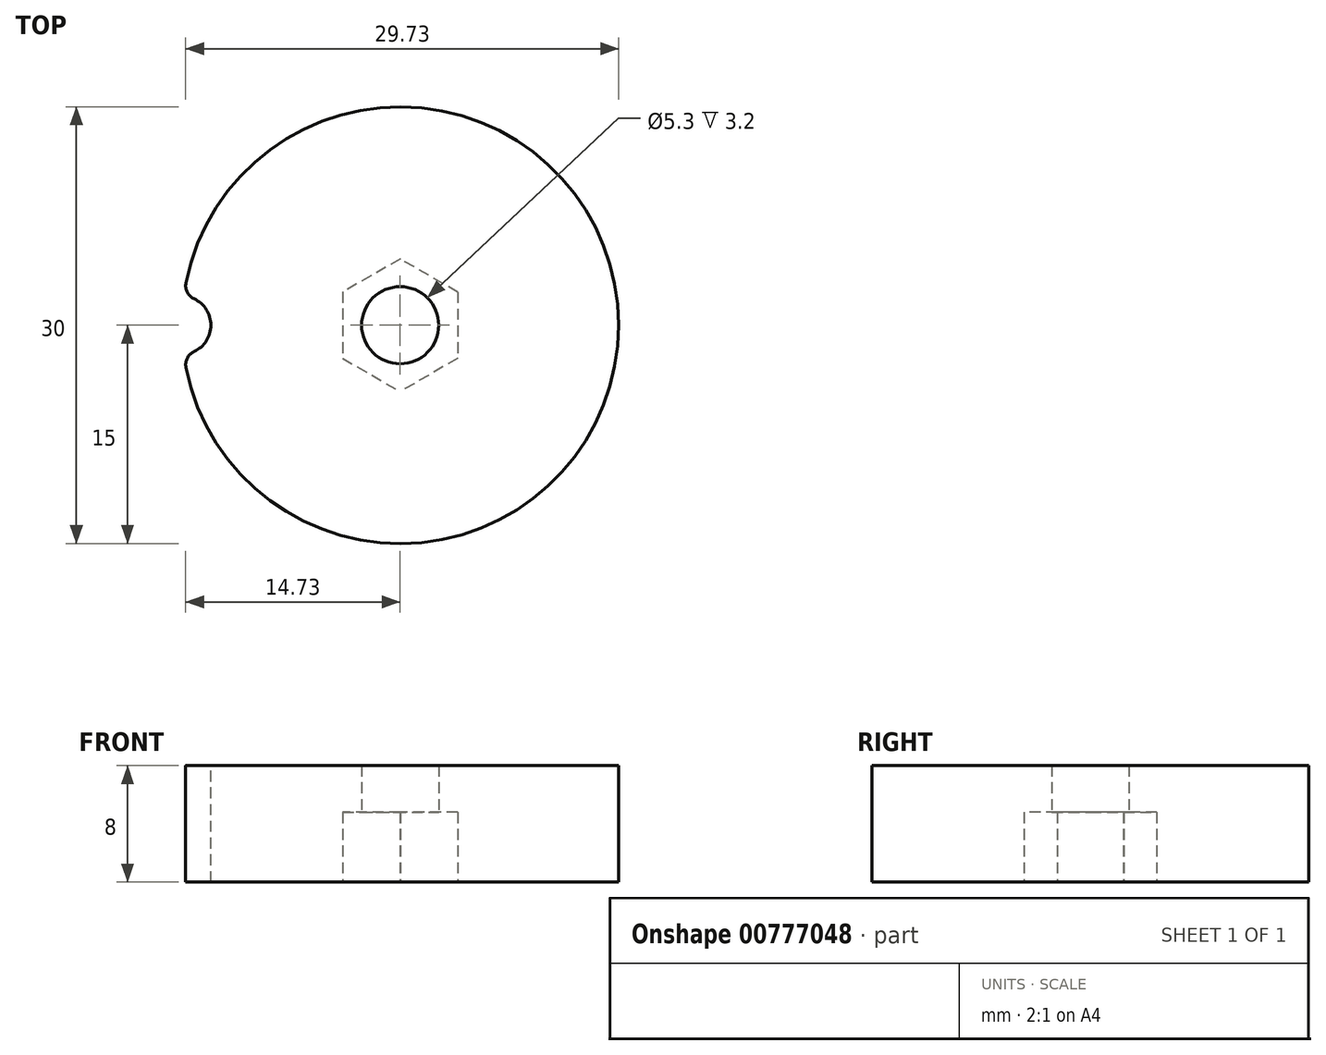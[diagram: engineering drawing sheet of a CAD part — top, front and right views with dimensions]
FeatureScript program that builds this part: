
annotation { "Feature Type Name" : "Feature", "Feature Type Description" : "" }
export const myFeature = defineFeature(function(context is Context, id is Id, definition is map)
    precondition{}
    {
        {
            var Q0;
            Q0=qCreatedBy(makeId("Top.planeOp"),FACE);
            var sketch = newSketch(context, id + "F0", { "sketchPlane" : qUnion([Q0])});
            skCircle(sketch, "E0", {"center": v(0, 0) * mm, "radius": 15 * mm});
            skCircle(sketch, "E1", {"center": v(0, 0) * mm, "radius": 2.65 * mm});
            skSolve(sketch);
        }
        {
            var Q0;
            Q0=qSketchRegion(id+"F0",true);
            extrude(context, id + "F1", {"entities" : qUnion([Q0]), "depth" : 8 * mm});
        }
        {
            var Q0;
            Q0=makeQuery(id+"F1.opExtrude","CAP_FACE",FACE,{"disambiguationData":[OSD([sQuery(id+"F0.wireOp",EDGE,"E0"),sQuery(id+"F0.wireOp",EDGE,"E1")])],"isStart":true});
            var sketch = newSketch(context, id + "F2", { "sketchPlane" : qUnion([Q0])});
            skPoint(sketch, "E2", {"position": v(0, 0) * mm});
            skCircle(sketch, "E3.0", {"center": v(0, 0) * mm, "radius": 2.65 * mm, "construction": true});
            skCircle(sketch, "E4", {"center": v(0, 0) * mm, "radius": 3.95 * mm, "construction": true});
            skLineSegment(sketch, "E5", {"start": v(-3.95, -2.29) * mm, "end": v(-3.95, 2.27) * mm});
            skLineSegment(sketch, "E6", {"start": v(-3.95, 2.27) * mm, "end": v(0, 4.56) * mm});
            skLineSegment(sketch, "E7", {"start": v(3.96, -2.28) * mm, "end": v(0, -4.56) * mm});
            skLineSegment(sketch, "E8", {"start": v(0, -4.56) * mm, "end": v(-3.95, -2.29) * mm});
            skLineSegment(sketch, "E9", {"start": v(3.96, -2.28) * mm, "end": v(3.94, 2.28) * mm});
            skLineSegment(sketch, "E10", {"start": v(3.94, 2.28) * mm, "end": v(0, 4.56) * mm});
            skSolve(sketch);
        }
        {
            var Q0;
            Q0=qSketchRegion(id+"F2",true);
            extrude(context, id + "F3", {"entities" : qUnion([Q0]), "operationType" : NewBodyOperationType.REMOVE, "oppositeDirection" : true, "depth" : 4.8 * mm});
        }
        {
            var Q0;
            Q0=makeQuery(id+"F1.opExtrude","CAP_FACE",FACE,{"disambiguationData":[OSD([sQuery(id+"F0.wireOp",EDGE,"E0"),sQuery(id+"F0.wireOp",EDGE,"E1")])],"isStart":false});
            var sketch = newSketch(context, id + "F4", { "sketchPlane" : qUnion([Q0])});
            skCircle(sketch, "E11", {"center": v(-15, 0) * mm, "radius": 2 * mm});
            skSolve(sketch);
        }
        {
            var Q0;
            Q0=qSketchRegion(id+"F4",true);
            extrude(context, id + "F5", {"entities" : qUnion([Q0]), "operationType" : NewBodyOperationType.REMOVE, "endBound" : BoundingType.THROUGH_ALL, "oppositeDirection" : true, "depth" : 25 * mm});
        }
        {
            var Q0;
            Q0=makeQuery(id+"F5.boolean.opBoolean","INTERSECT",EDGE,{"disambiguationData":[OD(1.0)],"derivedFrom":[makeQuery(id+"F1.opExtrude","SWEPT_FACE",FACE,{"disambiguationData":[OSD([sQuery(id+"F0.wireOp",EDGE,"E0")])]}),makeQuery(id+"F5.opExtrude","SWEPT_FACE",FACE,{"disambiguationData":[OSD([sQuery(id+"F4.wireOp",EDGE,"E11")])]})]});
            var Q1;
            Q1=makeQuery(id+"F5.boolean.opBoolean","INTERSECT",EDGE,{"disambiguationData":[OD(0.0)],"derivedFrom":[makeQuery(id+"F1.opExtrude","SWEPT_FACE",FACE,{"disambiguationData":[OSD([sQuery(id+"F0.wireOp",EDGE,"E0")])]}),makeQuery(id+"F5.opExtrude","SWEPT_FACE",FACE,{"disambiguationData":[OSD([sQuery(id+"F4.wireOp",EDGE,"E11")])]})]});
            fillet(context, id + "F6", {"entities" : qUnion([Q0, Q1]), "radius" : 1 * mm, "tangentPropagation" : true, "allowEdgeOverflow" : false});
        }
    });
